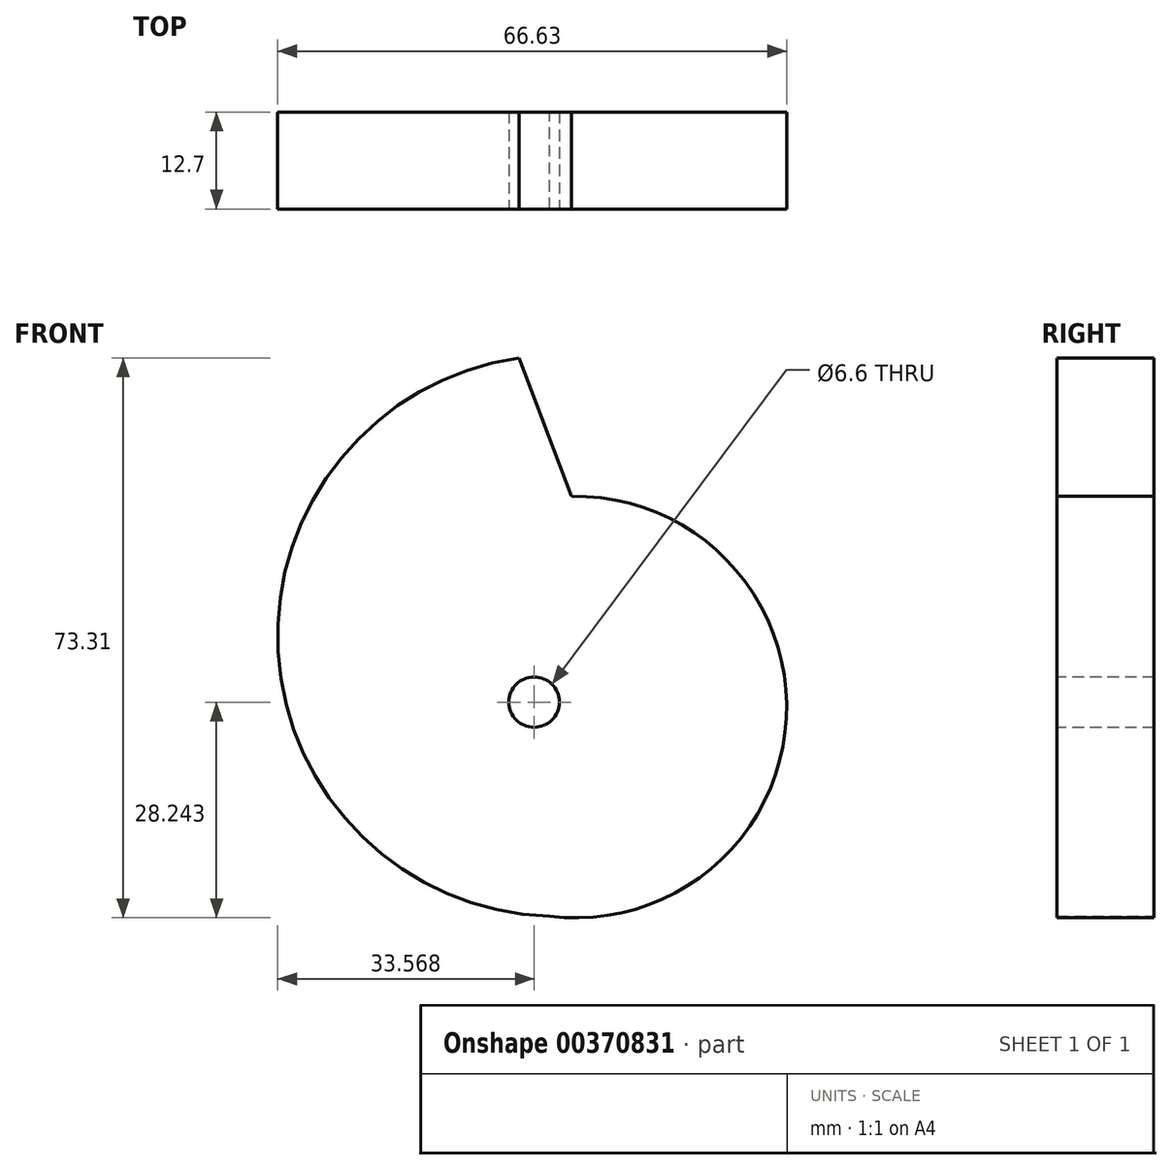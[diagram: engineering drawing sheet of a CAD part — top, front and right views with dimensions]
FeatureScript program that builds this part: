
annotation { "Feature Type Name" : "Feature", "Feature Type Description" : "" }
export const myFeature = defineFeature(function(context is Context, id is Id, definition is map)
    precondition{}
    {
        {
            var Q0;
            Q0=qCreatedBy(makeId("Front.planeOp"),FACE);
            var sketch = newSketch(context, id + "F0", { "sketchPlane" : qUnion([Q0])});
            skLineSegment(sketch, "E0", {"start": v(-41.44, 46.91) * mm, "end": v(-34.54, 28.78) * mm});
            skArc(sketch, "E1", {"start": v(-41.44, 46.91) * mm, "mid": v(-72.96, 8.51) * mm, "end": v(-37.41, -26.2) * mm});
            skArc(sketch, "E2", {"start": v(-37.41, -26.2) * mm, "mid": v(-6.43, -0.25) * mm, "end": v(-34.54, 28.78) * mm});
            skSolve(sketch);
        }
        {
            var Q0;
            Q0 = qSketchRegion(id + "F0", true);
            extrude(context, id + "F1", {"entities" : qUnion([Q0]), "depth" : 12.7 * mm});
        }
        {
            var Q0;
            Q0=makeQuery(id+"F1.opExtrude","CAP_FACE",FACE,{"disambiguationData":[OSD([sQuery(id+"F0.wireOp",EDGE,"E0"),sQuery(id+"F0.wireOp",EDGE,"E1"),sQuery(id+"F0.wireOp",EDGE,"E2")])],"isStart":false});
            var sketch = newSketch(context, id + "F2", { "sketchPlane" : qUnion([Q0])});
            skCircle(sketch, "E3", {"center": v(-39.45, 1.84) * mm, "radius": 3.3 * mm});
            skSolve(sketch);
        }
        {
            var Q0;
            Q0 = qSketchRegion(id + "F2", true);
            extrude(context, id + "F3", {"entities" : qUnion([Q0]), "operationType" : NewBodyOperationType.REMOVE, "oppositeDirection" : true, "depth" : 25.4 * mm});
        }
    });
